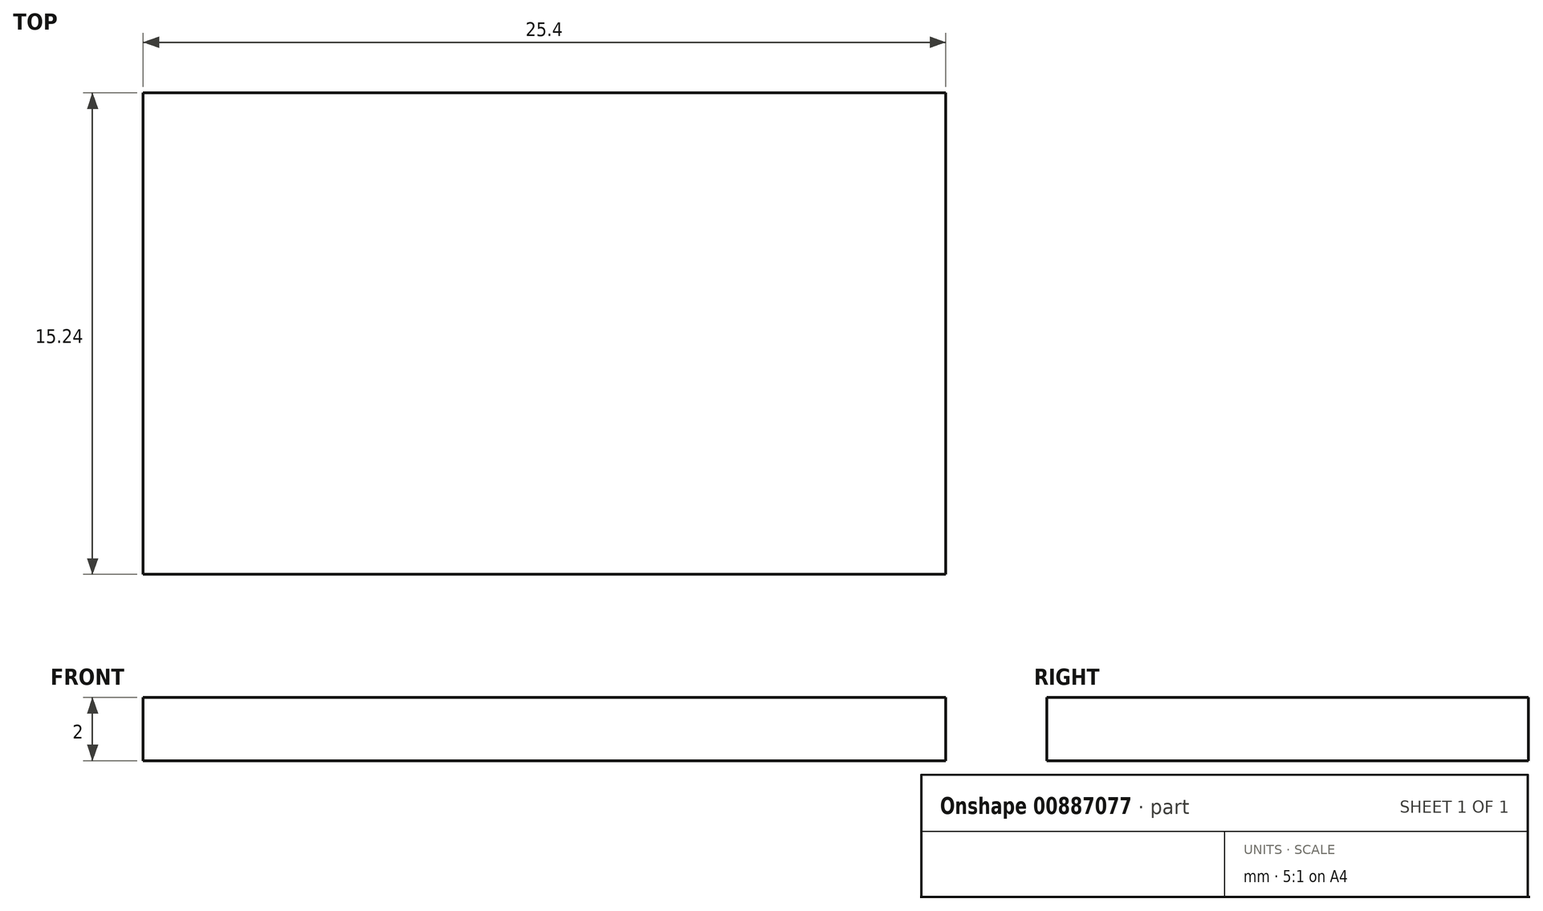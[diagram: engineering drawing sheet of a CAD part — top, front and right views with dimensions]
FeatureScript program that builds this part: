
annotation { "Feature Type Name" : "Feature", "Feature Type Description" : "" }
export const myFeature = defineFeature(function(context is Context, id is Id, definition is map)
    precondition{}
    {
        {
            var Q0;
            Q0=qCreatedBy(makeId("Top.planeOp"),FACE);
            var sketch = newSketch(context, id + "F0", { "sketchPlane" : qUnion([Q0])});
            skLineSegment(sketch, "E0.bottom", {"start": v(12.7, -7.62) * mm, "end": v(-12.7, -7.62) * mm});
            skLineSegment(sketch, "E0.top", {"start": v(12.7, 7.62) * mm, "end": v(-12.7, 7.62) * mm});
            skLineSegment(sketch, "E0.left", {"start": v(12.7, -7.62) * mm, "end": v(12.7, 7.62) * mm});
            skLineSegment(sketch, "E0.right", {"start": v(-12.7, -7.62) * mm, "end": v(-12.7, 7.62) * mm});
            skPoint(sketch, "E0.middle", {"position": v(0, 0) * mm});
            skSolve(sketch);
        }
        {
            var Q0;
            Q0=qSketchRegion(id+"F0",true);
            extrude(context, id + "F1", {"entities" : qUnion([Q0]), "depth" : 2 * mm, "offsetDistance" : 25 * mm});
        }
    });
